# Revit family: Sanitary_Installation-Systems_hansgrohe_13622USA-hansgrohe-Basic-set-for-single_87
name_source: partatom
category: Plumbing Fixtures
revit_build: Autodesk Revit 2018 (Build: 20170223_1515(x64)
units: mm (PartAtom-declared; Revit-internal decimal feet)

## family parameters
Cut with Voids When Loaded = Yes
Host = Face
OmniClass Number = 23.27.31.29.11
OmniClass Title = Manual Mixing Valves
Part Type = Normal
Room Calculation Point = No
Round Connector Dimension = Use Diameter
Shared = No

## types (1)
- 13622USA hansgrohe Basic set for single lever basin mixer for concealed installation wall-mounted
    BIMobject category = Installation Systems
    Connector Description = Water Inlet 1/2
    Default Elevation = 0' - 0"
    Description = hansgrohe Basic set for single lever basin mixer for concealed installation wall-mounted
    Design country = Germany
    Diameter = 0' - 0 1/2"
    EAN code = 4024718048822
    Edition number = 1
    IFC Classification = Sanitary Terminal
    Manufacturer = Hansgrohe
    Manufacturer country = Germany
    Manufacturer name = hansgrohe
    Material 1 = Hansgrohe - Plastic - Green
    Material 2 = Hansgrohe - Metal - Brass
    Material 3 = Hansgrohe - Plastic - Black
    Material 4 = Hansgrohe - Plastic - Transparent White
    Model = 13622USA
    OmniClass Code = 23-27 31 29 11
    OmniClass Description = Manual Mixing Valves
    Product Guid = 552d494d-8054-412a-96e7-988376493285
    Product SKU = 13622USA
    Product data url = https://bimobject.com
    Product family = hansgrohe
    Product group = Concealed Basic set washbasin mixer
    Product name = 13622USA hansgrohe Basic set for single lever basin mixer for concealed installation wall-mounted
    Product url = https://www.hansgrohe.com
    QR code = https://bimobject.com
    URL = http://www.hansgrohe-int.com
    Uniclass 2015 Code = Pr_40_20_96_81
    Uniclass 2015 Name = Sinks
    Weight Net (Kg) = 1

## geometry (parser evidence)
native form markers: Sweep x6
no freeform markers — native parametric forms only
